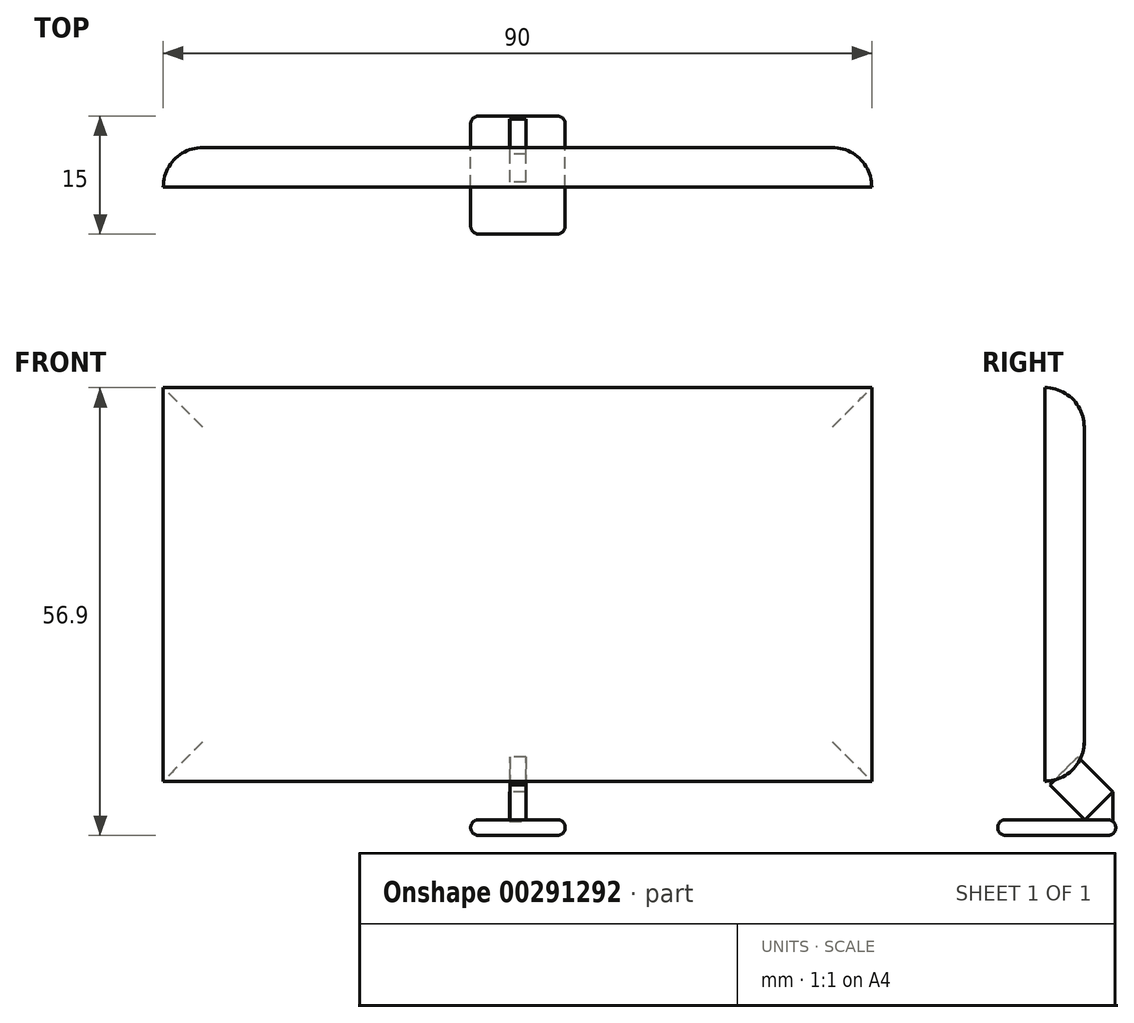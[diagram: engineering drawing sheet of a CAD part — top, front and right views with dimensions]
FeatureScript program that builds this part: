
annotation { "Feature Type Name" : "Feature", "Feature Type Description" : "" }
export const myFeature = defineFeature(function(context is Context, id is Id, definition is map)
    precondition{}
    {
        {
            var Q0;
            Q0=qCreatedBy(makeId("Front.planeOp"),FACE);
            var sketch = newSketch(context, id + "F0", { "sketchPlane" : qUnion([Q0])});
            skLineSegment(sketch, "E0.bottom", {"start": v(-45, 25) * mm, "end": v(45, 25) * mm});
            skLineSegment(sketch, "E0.top", {"start": v(-45, -25) * mm, "end": v(45, -25) * mm});
            skLineSegment(sketch, "E0.left", {"start": v(-45, 25) * mm, "end": v(-45, -25) * mm});
            skLineSegment(sketch, "E0.right", {"start": v(45, 25) * mm, "end": v(45, -25) * mm});
            skPoint(sketch, "E0.middle", {"position": v(0, 0) * mm});
            skLineSegment(sketch, "E1", {"start": v(0, -25) * mm, "end": v(-2.5, -25) * mm});
            skLineSegment(sketch, "E2", {"start": v(0, -25) * mm, "end": v(2.5, -25) * mm});
            skSolve(sketch);
        }
        {
            var Q0;
            Q0=makeQuery(id+"F0.imprint","IMPRINT",FACE,{"disambiguationData":[TD([[makeQuery(id+"F0.imprint","IMPRINT",EDGE,{"derivedFrom":sQuery(id+"F0.wireOp",EDGE,"E0.bottom")}),-1.0]])]});
            extrude(context, id + "F1", {"entities" : qUnion([Q0]), "oppositeDirection" : true, "depth" : 5 * mm});
        }
        {
            var Q0;
            Q0=makeQuery(id+"F1.opExtrude","CAP_FACE",FACE,{"disambiguationData":[OSD([sQuery(id+"F0.wireOp",EDGE,"E0.bottom"),sQuery(id+"F0.wireOp",EDGE,"E0.top"),sQuery(id+"F0.wireOp",EDGE,"E0.left"),sQuery(id+"F0.wireOp",EDGE,"E0.right"),sQuery(id+"F0.wireOp",EDGE,"E1"),sQuery(id+"F0.wireOp",EDGE,"E2")])],"isStart":false});
            var sketch = newSketch(context, id + "F2", { "sketchPlane" : qUnion([Q0])});
            skLineSegment(sketch, "E3", {"start": v(0, -25) * mm, "end": v(-2.5, -25) * mm});
            skLineSegment(sketch, "E4", {"start": v(0, -25) * mm, "end": v(2.5, -25) * mm});
            skLineSegment(sketch, "E5", {"start": v(-2.5, -25) * mm, "end": v(-2.5, -30) * mm});
            skLineSegment(sketch, "E6", {"start": v(-2.5, -30) * mm, "end": v(2.5, -30) * mm});
            skLineSegment(sketch, "E7", {"start": v(2.5, -30) * mm, "end": v(2.5, -25) * mm});
            skLineSegment(sketch, "E8", {"start": v(-2.5, -30) * mm, "end": v(-8.5, -30) * mm});
            skLineSegment(sketch, "E9", {"start": v(-8.5, -30) * mm, "end": v(-8.5, -33) * mm});
            skLineSegment(sketch, "E10", {"start": v(2.5, -30) * mm, "end": v(8.5, -30) * mm});
            skLineSegment(sketch, "E11", {"start": v(8.5, -30) * mm, "end": v(8.5, -33) * mm});
            skLineSegment(sketch, "E12", {"start": v(-8.5, -33) * mm, "end": v(8.5, -33) * mm});
            skSolve(sketch);
        }
        {
            var Q0;
            Q0=makeQuery(id+"F2.imprint","IMPRINT",FACE,{"disambiguationData":[TD([[makeQuery(id+"F2.imprint","IMPRINT",EDGE,{"derivedFrom":sQuery(id+"F2.wireOp",EDGE,"E6")}),-1.0]])]});
            extrude(context, id + "F3", {"entities" : qUnion([Q0]), "oppositeDirection" : true, "depth" : 15 * mm});
        }
        {
            var Q0;
            Q0=makeQuery(id+"F1.opExtrude","CAP_FACE",FACE,{"disambiguationData":[OSD([sQuery(id+"F0.wireOp",EDGE,"E0.bottom"),sQuery(id+"F0.wireOp",EDGE,"E0.top"),sQuery(id+"F0.wireOp",EDGE,"E0.left"),sQuery(id+"F0.wireOp",EDGE,"E0.right"),sQuery(id+"F0.wireOp",EDGE,"E1"),sQuery(id+"F0.wireOp",EDGE,"E2")])],"isStart":false});
            fillet(context, id + "F4", {"entities" : qUnion([Q0]), "radius" : 5 * mm, "tangentPropagation" : true, "allowEdgeOverflow" : false});
        }
        {
            var Q0;
            {var subQ0=sQuery(id+"F2.wireOp",EDGE,"E9");var subQ3=sQuery(id+"F2.wireOp",EDGE,"E10");var subQ4=sQuery(id+"F2.wireOp",EDGE,"E8");var subQ6=sQuery(id+"F2.wireOp",EDGE,"E6");Q0=makeQuery(id+"Fnu9TKGUWc5VBDW_1.boolean.opBoolean","SPLIT",EDGE,{"disambiguationData":[TD([makeQuery(id+"F3.opExtrude","SWEPT_FACE",FACE,{"disambiguationData":[OSD([subQ0])]})])],"derivedFrom":makeQuery(id+"F3.opExtrude","CAP_EDGE",EDGE,{"disambiguationData":[OSD([subQ6,subQ4,subQ3])],"isStart":true})});}
            cPlane(context, id + "F5", {"entities" : qUnion([Q0]), "cplaneType" : CPlaneType.LINE_ANGLE, "offset" : 25 * mm, "angle" : 45 * degree, "width" : 150 * mm, "height" : 150 * mm});
        }
        {
            var Q0;
            Q0=qCreatedBy(id+"F5.planeOp",FACE);
            var sketch = newSketch(context, id + "F6", { "sketchPlane" : qUnion([Q0])});
            skLineSegment(sketch, "E13", {"start": v(1.06, -17.55) * mm, "end": v(-0.94, -17.55) * mm});
            skLineSegment(sketch, "E14", {"start": v(1.06, -17.55) * mm, "end": v(1.06, -12.55) * mm});
            skLineSegment(sketch, "E15", {"start": v(-0.94, -17.55) * mm, "end": v(-0.94, -12.55) * mm});
            skLineSegment(sketch, "E16", {"start": v(1.06, -12.55) * mm, "end": v(-0.94, -12.55) * mm});
            skSolve(sketch);
        }
        {
            var Q0;
            Q0 = qSketchRegion(id + "F6", true);
            extrude(context, id + "F7", {"entities" : qUnion([Q0]), "depth" : 6.3 * mm});
        }
        {
            var Q0;
            Q0=makeQuery(id+"F3.opExtrude","SWEPT_BODY",BODY,{"disambiguationData":[OSD([sQuery(id+"F2.wireOp",EDGE,"E6"),sQuery(id+"F2.wireOp",EDGE,"E8"),sQuery(id+"F2.wireOp",EDGE,"E9"),sQuery(id+"F2.wireOp",EDGE,"E10"),sQuery(id+"F2.wireOp",EDGE,"E11"),sQuery(id+"F2.wireOp",EDGE,"E12")])]});
            deleteBodies(context, id + "F8", {"entities" : qUnion([Q0])});
        }
        {
            var Q0;
            Q0=qCreatedBy(makeId("Front.planeOp"),FACE);
            var sketch = newSketch(context, id + "F9", { "sketchPlane" : qUnion([Q0])});
            skPoint(sketch, "E17.0", {"position": v(1.06, -29.9) * mm});
            skPoint(sketch, "E18.0", {"position": v(-0.94, -29.9) * mm});
            skLineSegment(sketch, "E19", {"start": v(-0.94, -29.9) * mm, "end": v(-5.94, -29.9) * mm});
            skLineSegment(sketch, "E20", {"start": v(1.06, -29.9) * mm, "end": v(6.06, -29.9) * mm});
            skLineSegment(sketch, "E21", {"start": v(-0.94, -29.9) * mm, "end": v(1.06, -29.9) * mm});
            skLineSegment(sketch, "E22", {"start": v(-5.94, -29.9) * mm, "end": v(-5.94, -31.9) * mm});
            skLineSegment(sketch, "E23", {"start": v(-5.94, -31.9) * mm, "end": v(6.06, -31.9) * mm});
            skLineSegment(sketch, "E24", {"start": v(6.06, -31.9) * mm, "end": v(6.06, -29.9) * mm});
            skSolve(sketch);
        }
        {
            var Q0;
            Q0=makeQuery(id+"F9.imprint","IMPRINT",FACE,{"disambiguationData":[TD([[makeQuery(id+"F9.imprint","IMPRINT",EDGE,{"derivedFrom":sQuery(id+"F9.wireOp",EDGE,"E19")}),1.0]])]});
            extrude(context, id + "F10", {"entities" : qUnion([Q0]), "oppositeDirection" : true, "depth" : 9 * mm});
        }
        {
            var Q0;
            Q0=qCreatedBy(makeId("Right.planeOp"),FACE);
            var sketch = newSketch(context, id + "F11", { "sketchPlane" : qUnion([Q0])});
            skPoint(sketch, "E25.0", {"position": v(8.63, -26.37) * mm});
            skPoint(sketch, "E26.0", {"position": v(5.1, -29.9) * mm});
            skLineSegment(sketch, "E27", {"start": v(8.63, -26.37) * mm, "end": v(5.1, -29.9) * mm});
            skLineSegment(sketch, "E28", {"start": v(8.63, -26.37) * mm, "end": v(8.63, -29.9) * mm});
            skLineSegment(sketch, "E29", {"start": v(8.63, -29.9) * mm, "end": v(5.1, -29.9) * mm});
            skSolve(sketch);
        }
        {
            var Q0;
            Q0=makeQuery(id+"F11.imprint","IMPRINT",FACE,{"disambiguationData":[TD([[makeQuery(id+"F11.imprint","IMPRINT",EDGE,{"derivedFrom":sQuery(id+"F11.wireOp",EDGE,"E27")}),1.0]])]});
            extrude(context, id + "F12", {"entities" : qUnion([Q0]), "depth" : 1 * mm});
        }
        {
            var Q0;
            Q0=makeQuery(id+"F12.opExtrude","CAP_FACE",FACE,{"disambiguationData":[OSD([sQuery(id+"F11.wireOp",EDGE,"E27"),sQuery(id+"F11.wireOp",EDGE,"E28"),sQuery(id+"F11.wireOp",EDGE,"E29")])],"isStart":true});
            extrude(context, id + "F13", {"entities" : qUnion([Q0]), "depth" : 1 * mm});
        }
        {
            var Q0;
            Q0=makeQuery(id+"F10.opExtrude","CAP_FACE",FACE,{"disambiguationData":[OSD([sQuery(id+"F9.wireOp",EDGE,"E19"),sQuery(id+"F9.wireOp",EDGE,"E20"),sQuery(id+"F9.wireOp",EDGE,"E21"),sQuery(id+"F9.wireOp",EDGE,"E22"),sQuery(id+"F9.wireOp",EDGE,"E23"),sQuery(id+"F9.wireOp",EDGE,"E24")])],"isStart":false});
            extrude(context, id + "F14", {"entities" : qUnion([Q0]), "operationType" : NewBodyOperationType.ADD, "oppositeDirection" : true, "depth" : 15 * mm});
        }
        {
            var Q0;
            {var subQ0=sQuery(id+"F9.wireOp",EDGE,"E24");Q0=makeQuery(id+"F14.boolean.opBoolean","MERGE",FACE,{"derivedFrom":[makeQuery(id+"F10.opExtrude","SWEPT_FACE",FACE,{"disambiguationData":[OSD([subQ0])]}),makeQuery(id+"F14.opExtrude","SWEPT_FACE",FACE,{"disambiguationData":[OSD([subQ0])]})]});}
            fillet(context, id + "F15", {"entities" : qUnion([Q0]), "radius" : 1 * mm, "tangentPropagation" : true, "allowEdgeOverflow" : false});
        }
        {
            var Q0;
            Q0=makeQuery(id+"F10.opExtrude","CAP_FACE",FACE,{"disambiguationData":[OSD([sQuery(id+"F9.wireOp",EDGE,"E19"),sQuery(id+"F9.wireOp",EDGE,"E20"),sQuery(id+"F9.wireOp",EDGE,"E21"),sQuery(id+"F9.wireOp",EDGE,"E22"),sQuery(id+"F9.wireOp",EDGE,"E23"),sQuery(id+"F9.wireOp",EDGE,"E24")])],"isStart":false});
            fillet(context, id + "F16", {"entities" : qUnion([Q0]), "radius" : 1 * mm, "tangentPropagation" : true, "allowEdgeOverflow" : false});
        }
        {
            var Q0;
            {var subQ0=sQuery(id+"F9.wireOp",EDGE,"E22");Q0=makeQuery(id+"F14.boolean.opBoolean","MERGE",FACE,{"derivedFrom":[makeQuery(id+"F10.opExtrude","SWEPT_FACE",FACE,{"disambiguationData":[OSD([subQ0])]}),makeQuery(id+"F14.opExtrude","SWEPT_FACE",FACE,{"disambiguationData":[OSD([subQ0])]})]});}
            fillet(context, id + "F17", {"entities" : qUnion([Q0]), "radius" : 1 * mm, "tangentPropagation" : true, "allowEdgeOverflow" : false});
        }
        {
            var Q0;
            Q0=makeQuery(id+"F14.opExtrude","CAP_FACE",FACE,{"disambiguationData":[OSD([sQuery(id+"F9.wireOp",EDGE,"E19"),sQuery(id+"F9.wireOp",EDGE,"E20"),sQuery(id+"F9.wireOp",EDGE,"E21"),sQuery(id+"F9.wireOp",EDGE,"E22"),sQuery(id+"F9.wireOp",EDGE,"E23"),sQuery(id+"F9.wireOp",EDGE,"E24")])],"isStart":false});
            fillet(context, id + "F18", {"entities" : qUnion([Q0]), "radius" : 1 * mm, "tangentPropagation" : true, "allowEdgeOverflow" : false});
        }
    });
